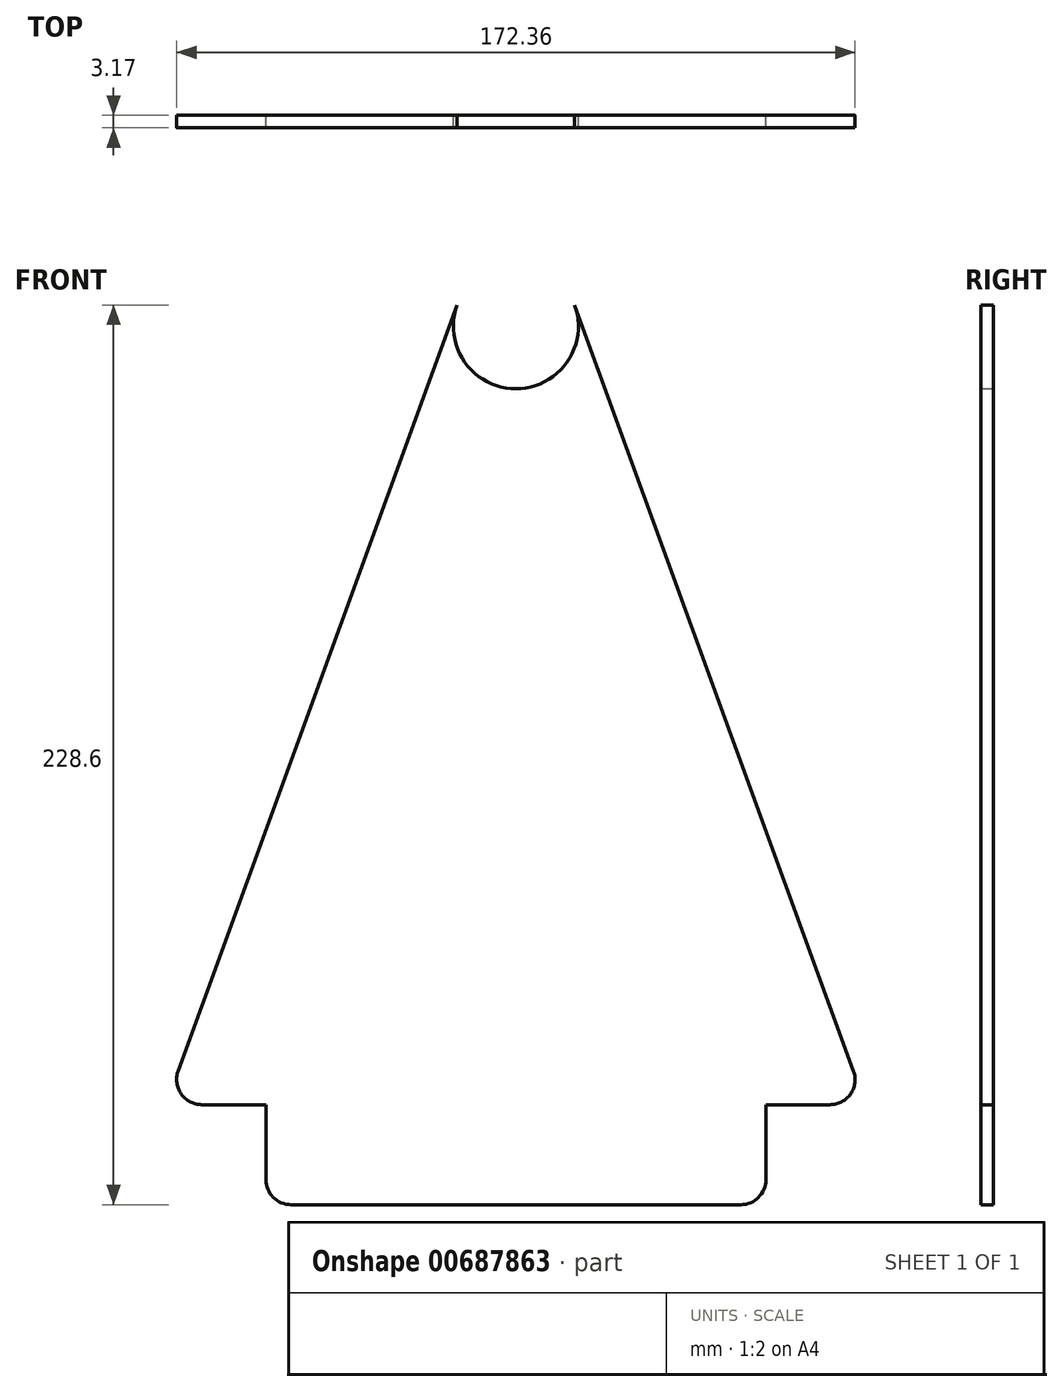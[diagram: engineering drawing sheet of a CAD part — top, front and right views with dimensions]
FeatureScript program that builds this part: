
annotation { "Feature Type Name" : "Feature", "Feature Type Description" : "" }
export const myFeature = defineFeature(function(context is Context, id is Id, definition is map)
    precondition{}
    {
        {
            var Q0;
            Q0=qCreatedBy(makeId("Front.planeOp"),FACE);
            var sketch = newSketch(context, id + "F0", { "sketchPlane" : qUnion([Q0])});
            skLineSegment(sketch, "E0.bottom", {"start": v(57.15, -63.77) * mm, "end": v(-57.15, -63.77) * mm});
            skLineSegment(sketch, "E0.top", {"start": v(63.5, -38.37) * mm, "end": v(-63.5, -38.37) * mm});
            skLineSegment(sketch, "E0.left", {"start": v(63.5, -57.42) * mm, "end": v(63.5, -38.37) * mm});
            skLineSegment(sketch, "E0.right", {"start": v(-63.5, -57.42) * mm, "end": v(-63.5, -38.37) * mm});
            skPoint(sketch, "E0.middle", {"position": v(0, -51.07) * mm});
            skLineSegment(sketch, "E1", {"start": v(-63.5, -38.37) * mm, "end": v(-79.83, -38.37) * mm});
            skLineSegment(sketch, "E2", {"start": v(63.5, -38.37) * mm, "end": v(79.83, -38.37) * mm});
            skPoint(sketch, "E3.center.orphan", {"position": v(0, 119.31) * mm});
            skPoint(sketch, "E4.end.orphan", {"position": v(-81.76, 159.4) * mm});
            skPoint(sketch, "E5.end.orphan", {"position": v(13.74, 126.35) * mm});
            skArc(sketch, "E6", {"start": v(-14.92, 164.83) * mm, "mid": v(0, 143.52) * mm, "end": v(14.92, 164.83) * mm});
            skLineSegment(sketch, "E7", {"start": v(-85.8, -29.85) * mm, "end": v(-14.92, 164.83) * mm});
            skLineSegment(sketch, "E8", {"start": v(85.8, -29.85) * mm, "end": v(14.92, 164.83) * mm});
            skPoint(sketch, "E9.visualSharp", {"position": v(-88.9, -38.37) * mm});
            skArc(sketch, "E9.filletArc", {"start": v(-85.8, -29.85) * mm, "mid": v(-85.03, -35.66) * mm, "end": v(-79.83, -38.37) * mm});
            skPoint(sketch, "E10.visualSharp", {"position": v(88.9, -38.37) * mm});
            skArc(sketch, "E10.filletArc", {"start": v(79.83, -38.37) * mm, "mid": v(85.03, -35.66) * mm, "end": v(85.8, -29.85) * mm});
            skPoint(sketch, "E11.visualSharp", {"position": v(63.5, -63.77) * mm});
            skArc(sketch, "E11.filletArc", {"start": v(57.15, -63.77) * mm, "mid": v(61.64, -61.9) * mm, "end": v(63.5, -57.42) * mm});
            skPoint(sketch, "E12.visualSharp", {"position": v(-63.5, -63.77) * mm});
            skArc(sketch, "E12.filletArc", {"start": v(-63.5, -57.42) * mm, "mid": v(-61.64, -61.9) * mm, "end": v(-57.15, -63.77) * mm});
            skLineSegment(sketch, "E13", {"start": v(79.83, -38.37) * mm, "end": v(-79.83, -38.37) * mm});
            skPoint(sketch, "E14.sketch_text.ascent.end.orphan", {"position": v(50.8, 17.28) * mm});
            skPoint(sketch, "E14.sketch_text.center.start.orphan", {"position": v(0, -12.97) * mm});
            skPoint(sketch, "E14.sketch_text.left.end.orphan", {"position": v(-50.8, 17.28) * mm});
            skSolve(sketch);
        }
        {
            var Q0;
            Q0 = qSketchRegion(id + "F0", true);
            extrude(context, id + "F1", {"entities" : qUnion([Q0]), "depth" : 3.17 * mm, "offsetDistance" : 25.4 * mm});
        }
    });
